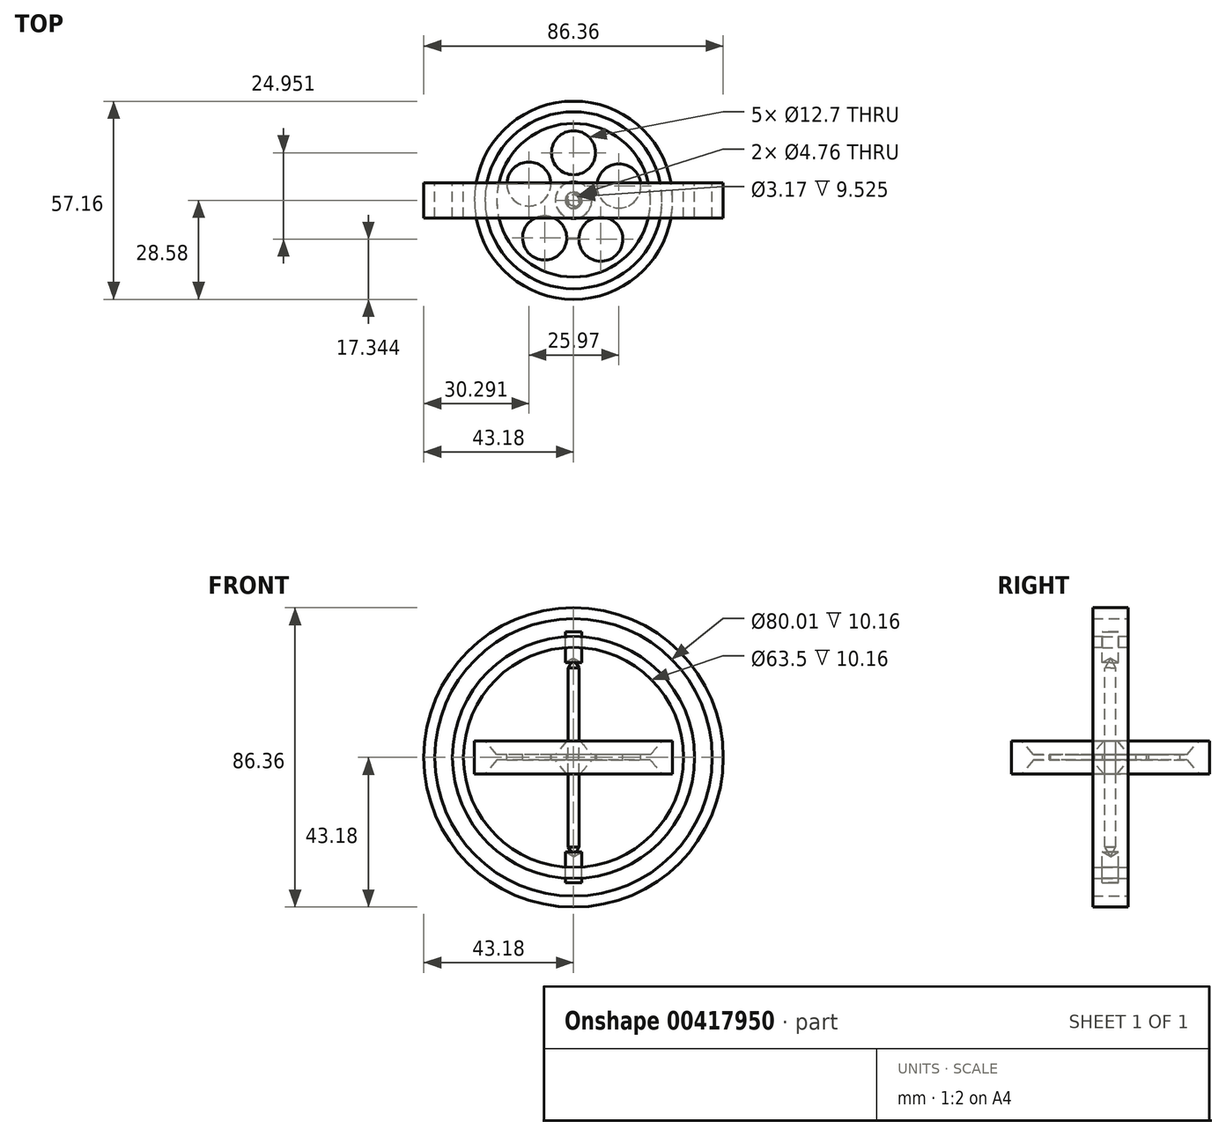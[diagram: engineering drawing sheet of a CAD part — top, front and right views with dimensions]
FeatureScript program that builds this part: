
annotation { "Feature Type Name" : "Feature", "Feature Type Description" : "" }
export const myFeature = defineFeature(function(context is Context, id is Id, definition is map)
    precondition{}
    {
        {
            var Q0;
            Q0=qCreatedBy(makeId("Front.planeOp"),FACE);
            var sketch = newSketch(context, id + "F0", { "sketchPlane" : qUnion([Q0])});
            skCircle(sketch, "E0", {"center": v(0, 0) * mm, "radius": 31.75 * mm});
            skCircle(sketch, "E1.0", {"center": v(0, 0) * mm, "radius": 34.92 * mm});
            skLineSegment(sketch, "E2", {"start": v(-28.58, 0) * mm, "end": v(-28.58, 4.76) * mm});
            skLineSegment(sketch, "E3", {"start": v(-28.58, 4.76) * mm, "end": v(-25.53, 4.76) * mm});
            skLineSegment(sketch, "E4", {"start": v(-25.53, 4.76) * mm, "end": v(-22.17, 0.76) * mm});
            skLineSegment(sketch, "E5", {"start": v(-22.17, 0.76) * mm, "end": v(-5.26, 0.76) * mm});
            skLineSegment(sketch, "E6", {"start": v(-5.26, 0.76) * mm, "end": v(-1.9, 4.76) * mm});
            skLineSegment(sketch, "E7", {"start": v(-1.9, 4.76) * mm, "end": v(0, 4.76) * mm});
            skLineSegment(sketch, "E8.MirrorCS", {"start": v(-28.58, 0) * mm, "end": v(-28.58, -4.76) * mm});
            skLineSegment(sketch, "E9.MirrorCS", {"start": v(-28.58, -4.76) * mm, "end": v(-25.53, -4.76) * mm});
            skLineSegment(sketch, "E10.MirrorCS", {"start": v(-25.53, -4.76) * mm, "end": v(-22.17, -0.76) * mm});
            skLineSegment(sketch, "E11.MirrorCS", {"start": v(-22.17, -0.76) * mm, "end": v(-5.26, -0.76) * mm});
            skLineSegment(sketch, "E12.MirrorCS", {"start": v(-5.26, -0.76) * mm, "end": v(-1.9, -4.76) * mm});
            skLineSegment(sketch, "E13.MirrorCS", {"start": v(-1.9, -4.76) * mm, "end": v(0, -4.76) * mm});
            skLineSegment(sketch, "E14", {"start": v(0, 4.76) * mm, "end": v(0, -4.76) * mm});
            skSolve(sketch);
        }
        {
            var Q0;
            Q0=makeQuery(id+"F0.imprint","IMPRINT",FACE,{"disambiguationData":[TD([[makeQuery(id+"F0.imprint","IMPRINT",EDGE,{"derivedFrom":sQuery(id+"F0.wireOp",EDGE,"E0")}),-1.0]])]});
            extrude(context, id + "F1", {"entities" : qUnion([Q0]), "endBound" : BoundingType.SYMMETRIC, "depth" : 10.16 * mm});
        }
        {
            var Q0;
            Q0=makeQuery(id+"F0.imprint","IMPRINT",FACE,{"disambiguationData":[TD([[makeQuery(id+"F0.imprint","IMPRINT",EDGE,{"derivedFrom":sQuery(id+"F0.wireOp",EDGE,"E2")}),-1.0]])]});
            var Q1;
            Q1=sQuery(id+"F0.wireOp",EDGE,"E14");
            revolve(context, id + "F2", {"entities" : qUnion([Q0]), "axis" : qUnion([Q1]), "revolveType" : RevolveType.FULL});
        }
        {
            var Q0;
            Q0=makeQuery(id+"F2.opRevolve","SWEPT_FACE",FACE,{"disambiguationData":[OSD([sQuery(id+"F0.wireOp",EDGE,"E7")])]});
            var sketch = newSketch(context, id + "F3", { "sketchPlane" : qUnion([Q0])});
            skCircle(sketch, "E15", {"center": v(0, 0) * mm, "radius": 1.53 * mm});
            skSolve(sketch);
        }
        {
            var Q0;
            Q0=sQuery(id+"F3.wireOp",VERTEX,"E15.center");
            var Q1;
            Q1=makeQuery(id+"F2.opRevolve","SWEPT_BODY",BODY,{"disambiguationData":[OSD([sQuery(id+"F0.wireOp",EDGE,"E2"),sQuery(id+"F0.wireOp",EDGE,"E3"),sQuery(id+"F0.wireOp",EDGE,"E4"),sQuery(id+"F0.wireOp",EDGE,"E5"),sQuery(id+"F0.wireOp",EDGE,"E6"),sQuery(id+"F0.wireOp",EDGE,"E7"),sQuery(id+"F0.wireOp",EDGE,"E8.MirrorCS"),sQuery(id+"F0.wireOp",EDGE,"E9.MirrorCS"),sQuery(id+"F0.wireOp",EDGE,"E10.MirrorCS"),sQuery(id+"F0.wireOp",EDGE,"E11.MirrorCS"),sQuery(id+"F0.wireOp",EDGE,"E12.MirrorCS"),sQuery(id+"F0.wireOp",EDGE,"E13.MirrorCS"),sQuery(id+"F0.wireOp",EDGE,"E14")])]});
            hole(context, id + "F4", {"style" : HoleStyle.SIMPLE, "endStyle" : HoleEndStyle.THROUGH, "holeDiameter" : 3.17 * mm, "isTappedThrough" : true, "tappedDepth" : 12.7 * mm, "tapClearance" : 3, "startFromSketch" : true, "locations" : qUnion([Q0]), "scope" : qUnion([Q1])});
        }
        {
            var Q0;
            Q0=qCreatedBy(makeId("Front.planeOp"),FACE);
            var sketch = newSketch(context, id + "F5", { "sketchPlane" : qUnion([Q0])});
            skLineSegment(sketch, "E16", {"start": v(0, 0) * mm, "end": v(0, -28.58) * mm});
            skLineSegment(sketch, "E17", {"start": v(0, -28.58) * mm, "end": v(-1.59, -25.83) * mm});
            skLineSegment(sketch, "E18", {"start": v(-1.59, -25.83) * mm, "end": v(-1.59, 0) * mm});
            skLineSegment(sketch, "E19", {"start": v(-1.59, 0) * mm, "end": v(0, 0) * mm});
            skLineSegment(sketch, "E20.MirrorCS", {"start": v(-1.59, 25.83) * mm, "end": v(-1.59, 0) * mm});
            skLineSegment(sketch, "E21.MirrorCS", {"start": v(0, 28.58) * mm, "end": v(-1.59, 25.83) * mm});
            skLineSegment(sketch, "E22.MirrorCS", {"start": v(0, 0) * mm, "end": v(0, 28.58) * mm});
            skSolve(sketch);
        }
        {
            var Q0;
            Q0=makeQuery(id+"F5.imprint","IMPRINT",FACE,{"disambiguationData":[TD([[makeQuery(id+"F5.imprint","IMPRINT",EDGE,{"derivedFrom":sQuery(id+"F5.wireOp",EDGE,"E19")}),1.0]])]});
            var Q1;
            Q1=makeQuery(id+"F5.imprint","IMPRINT",FACE,{"disambiguationData":[TD([[makeQuery(id+"F5.imprint","IMPRINT",EDGE,{"derivedFrom":sQuery(id+"F5.wireOp",EDGE,"E16")}),-1.0]])]});
            var Q2;
            Q2=sQuery(id+"F5.wireOp",EDGE,"E16");
            revolve(context, id + "F6", {"entities" : qUnion([Q0, Q1]), "axis" : qUnion([Q2]), "revolveType" : RevolveType.FULL});
        }
        {
            var Q0;
            Q0=makeQuery(id+"F2.opRevolve","SWEPT_FACE",FACE,{"disambiguationData":[OSD([sQuery(id+"F0.wireOp",EDGE,"E5")])]});
            var sketch = newSketch(context, id + "F7", { "sketchPlane" : qUnion([Q0])});
            skCircle(sketch, "E23", {"center": v(0, 13.72) * mm, "radius": 6.35 * mm});
            skLineSegment(sketch, "E24", {"start": v(0, 22.17) * mm, "end": v(0, 5.26) * mm});
            skCircle(sketch, "E25.1.0", {"center": v(13.08, 4.12) * mm, "radius": 6.35 * mm});
            skCircle(sketch, "E25.2.0", {"center": v(7.87, -11.24) * mm, "radius": 6.35 * mm});
            skCircle(sketch, "E25.3.0", {"center": v(-8.35, -10.88) * mm, "radius": 6.35 * mm});
            skCircle(sketch, "E25.4.0", {"center": v(-12.89, 4.7) * mm, "radius": 6.35 * mm});
            skPoint(sketch, "E25.center", {"position": v(0, 0) * mm});
            skLineSegment(sketch, "E25.anchor1", {"start": v(0, 0) * mm, "end": v(0, 13.72) * mm, "construction": true});
            skLineSegment(sketch, "E25.anchor2", {"start": v(0, 0) * mm, "end": v(-12.89, 4.7) * mm, "construction": true});
            skSolve(sketch);
        }
        {
            var Q0;
            Q0=sQuery(id+"F7.wireOp",VERTEX,"E25.4.0.center");
            var Q1;
            Q1=sQuery(id+"F7.wireOp",VERTEX,"E23.center");
            var Q2;
            Q2=sQuery(id+"F7.wireOp",VERTEX,"E25.1.0.center");
            var Q3;
            Q3=sQuery(id+"F7.wireOp",VERTEX,"E25.2.0.center");
            var Q4;
            Q4=sQuery(id+"F7.wireOp",VERTEX,"E25.3.0.center");
            var Q5;
            Q5=makeQuery(id+"F2.opRevolve","SWEPT_BODY",BODY,{"disambiguationData":[OSD([sQuery(id+"F0.wireOp",EDGE,"E2"),sQuery(id+"F0.wireOp",EDGE,"E3"),sQuery(id+"F0.wireOp",EDGE,"E4"),sQuery(id+"F0.wireOp",EDGE,"E5"),sQuery(id+"F0.wireOp",EDGE,"E6"),sQuery(id+"F0.wireOp",EDGE,"E7"),sQuery(id+"F0.wireOp",EDGE,"E8.MirrorCS"),sQuery(id+"F0.wireOp",EDGE,"E9.MirrorCS"),sQuery(id+"F0.wireOp",EDGE,"E10.MirrorCS"),sQuery(id+"F0.wireOp",EDGE,"E11.MirrorCS"),sQuery(id+"F0.wireOp",EDGE,"E12.MirrorCS"),sQuery(id+"F0.wireOp",EDGE,"E13.MirrorCS"),sQuery(id+"F0.wireOp",EDGE,"E14")])]});
            hole(context, id + "F8", {"style" : HoleStyle.SIMPLE, "endStyle" : HoleEndStyle.THROUGH, "holeDiameter" : 12.7 * mm, "isTappedThrough" : true, "tappedDepth" : 12.7 * mm, "tapClearance" : 3, "startFromSketch" : true, "locations" : qUnion([Q0, Q1, Q2, Q3, Q4]), "scope" : qUnion([Q5])});
        }
        {
            var Q0;
            Q0=qCreatedBy(makeId("Top.planeOp"),FACE);
            var sketch = newSketch(context, id + "F9", { "sketchPlane" : qUnion([Q0])});
            skCircle(sketch, "E26", {"center": v(0, 0) * mm, "radius": 2.38 * mm});
            skSolve(sketch);
        }
        {
            var Q0;
            Q0=sQuery(id+"F9.wireOp",VERTEX,"E26.center");
            var Q1;
            Q1=makeQuery(id+"F1.opExtrude","SWEPT_BODY",BODY,{"disambiguationData":[OSD([sQuery(id+"F0.wireOp",EDGE,"E0"),sQuery(id+"F0.wireOp",EDGE,"E1.0")])]});
            hole(context, id + "F10", {"style" : HoleStyle.SIMPLE, "endStyle" : HoleEndStyle.THROUGH, "oppositeDirection" : true, "holeDiameter" : 4.76 * mm, "isTappedThrough" : true, "tappedDepth" : 12.7 * mm, "tapClearance" : 3, "startFromSketch" : true, "locations" : qUnion([Q0]), "scope" : qUnion([Q1])});
        }
        {
            var Q0;
            Q0=sQuery(id+"F9.wireOp",VERTEX,"E26.center");
            var Q1;
            Q1=makeQuery(id+"F1.opExtrude","SWEPT_BODY",BODY,{"disambiguationData":[OSD([sQuery(id+"F0.wireOp",EDGE,"E0"),sQuery(id+"F0.wireOp",EDGE,"E1.0")])]});
            hole(context, id + "F11", {"style" : HoleStyle.SIMPLE, "endStyle" : HoleEndStyle.THROUGH, "holeDiameter" : 4.76 * mm, "isTappedThrough" : true, "tappedDepth" : 12.7 * mm, "tapClearance" : 3, "startFromSketch" : true, "locations" : qUnion([Q0]), "scope" : qUnion([Q1])});
        }
        {
            var Q0;
            Q0=qCreatedBy(makeId("Front.planeOp"),FACE);
            var sketch = newSketch(context, id + "F12", { "sketchPlane" : qUnion([Q0])});
            skLineSegment(sketch, "E27", {"start": v(0, 28.67) * mm, "end": v(-2.38, 27.3) * mm});
            skLineSegment(sketch, "E28", {"start": v(-2.38, 27.3) * mm, "end": v(-2.38, 36.18) * mm});
            skLineSegment(sketch, "E29", {"start": v(-2.38, 36.18) * mm, "end": v(0, 36.18) * mm});
            skLineSegment(sketch, "E30", {"start": v(0, 36.18) * mm, "end": v(0, 28.67) * mm});
            skLineSegment(sketch, "E31.MirrorCS", {"start": v(0, -36.18) * mm, "end": v(0, -28.67) * mm});
            skLineSegment(sketch, "E32.MirrorCS", {"start": v(-2.38, -36.18) * mm, "end": v(0, -36.18) * mm});
            skLineSegment(sketch, "E33.MirrorCS", {"start": v(-2.38, -27.3) * mm, "end": v(-2.38, -36.18) * mm});
            skLineSegment(sketch, "E34.MirrorCS", {"start": v(0, -28.67) * mm, "end": v(-2.38, -27.3) * mm});
            skSolve(sketch);
        }
        {
            var Q0;
            Q0=makeQuery(id+"F12.imprint","IMPRINT",FACE,{"disambiguationData":[TD([[makeQuery(id+"F12.imprint","IMPRINT",EDGE,{"derivedFrom":sQuery(id+"F12.wireOp",EDGE,"E27")}),-1.0]])]});
            var Q1;
            Q1=makeQuery(id+"F12.imprint","IMPRINT",FACE,{"disambiguationData":[TD([[makeQuery(id+"F12.imprint","IMPRINT",EDGE,{"derivedFrom":sQuery(id+"F12.wireOp",EDGE,"E31.MirrorCS")}),1.0]])]});
            var Q2;
            Q2=sQuery(id+"F12.wireOp",EDGE,"E30");
            revolve(context, id + "F13", {"entities" : qUnion([Q0, Q1]), "axis" : qUnion([Q2]), "revolveType" : RevolveType.FULL});
        }
        {
            var Q0;
            Q0=qCreatedBy(makeId("Front.planeOp"),FACE);
            var sketch = newSketch(context, id + "F14", { "sketchPlane" : qUnion([Q0])});
            skCircle(sketch, "E35", {"center": v(0, 0) * mm, "radius": 43.18 * mm});
            skCircle(sketch, "E36.0", {"center": v(0, 0) * mm, "radius": 40 * mm});
            skSolve(sketch);
        }
        {
            var Q0;
            Q0=makeQuery(id+"F14.imprint","IMPRINT",FACE,{"disambiguationData":[TD([[makeQuery(id+"F14.imprint","IMPRINT",EDGE,{"derivedFrom":sQuery(id+"F14.wireOp",EDGE,"E35")}),1.0]])]});
            extrude(context, id + "F15", {"entities" : qUnion([Q0]), "endBound" : BoundingType.SYMMETRIC, "depth" : 10.16 * mm});
        }
    });
